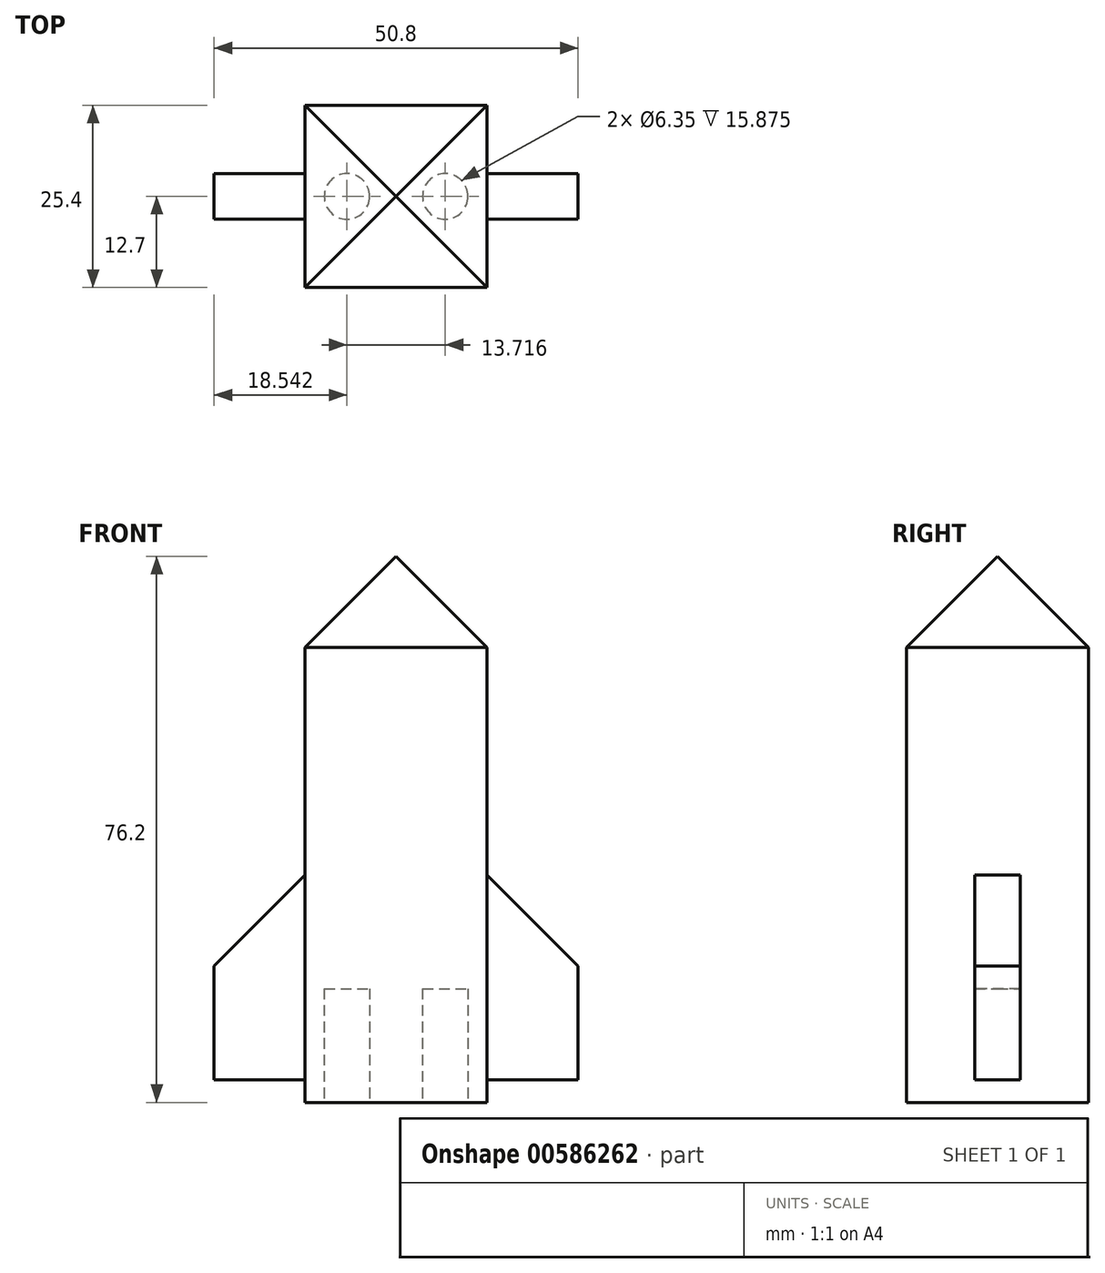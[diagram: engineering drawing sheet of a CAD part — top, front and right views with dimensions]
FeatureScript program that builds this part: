
annotation { "Feature Type Name" : "Feature", "Feature Type Description" : "" }
export const myFeature = defineFeature(function(context is Context, id is Id, definition is map)
    precondition{}
    {
        {
            var Q0;
            Q0=qCreatedBy(makeId("Front.planeOp"),FACE);
            var sketch = newSketch(context, id + "F0", { "sketchPlane" : qUnion([Q0])});
            skLineSegment(sketch, "E0.bottom", {"start": v(-25.4, 0) * mm, "end": v(25.4, 0) * mm, "construction": true});
            skLineSegment(sketch, "E0.top", {"start": v(-25.4, 76.2) * mm, "end": v(25.4, 76.2) * mm, "construction": true});
            skLineSegment(sketch, "E0.left", {"start": v(-25.4, 0) * mm, "end": v(-25.4, 76.2) * mm, "construction": true});
            skLineSegment(sketch, "E0.right", {"start": v(25.4, 0) * mm, "end": v(25.4, 76.2) * mm, "construction": true});
            skLineSegment(sketch, "E1", {"start": v(0, 0) * mm, "end": v(0, 76.2) * mm, "construction": true});
            skLineSegment(sketch, "E2", {"start": v(0, 76.2) * mm, "end": v(-12.7, 63.5) * mm});
            skLineSegment(sketch, "E3", {"start": v(-12.7, 63.5) * mm, "end": v(-12.7, 31.75) * mm});
            skLineSegment(sketch, "E4", {"start": v(-12.7, 31.75) * mm, "end": v(-25.4, 19.05) * mm});
            skLineSegment(sketch, "E5", {"start": v(-25.4, 3.18) * mm, "end": v(-12.7, 3.18) * mm});
            skLineSegment(sketch, "E6", {"start": v(-12.7, 3.18) * mm, "end": v(-12.7, 0) * mm});
            skLineSegment(sketch, "E7", {"start": v(-12.7, 0) * mm, "end": v(0, 0) * mm});
            skLineSegment(sketch, "E8", {"start": v(-25.4, 19.05) * mm, "end": v(-25.4, 3.18) * mm});
            skLineSegment(sketch, "E9.MirrorCS", {"start": v(12.7, 0) * mm, "end": v(0, 0) * mm});
            skLineSegment(sketch, "E10.MirrorCS", {"start": v(12.7, 3.18) * mm, "end": v(12.7, 0) * mm});
            skLineSegment(sketch, "E11.MirrorCS", {"start": v(25.4, 3.17) * mm, "end": v(12.7, 3.18) * mm});
            skLineSegment(sketch, "E12.MirrorCS", {"start": v(25.4, 19.05) * mm, "end": v(25.4, 3.18) * mm});
            skLineSegment(sketch, "E13.MirrorCS", {"start": v(12.7, 31.75) * mm, "end": v(25.4, 19.05) * mm});
            skLineSegment(sketch, "E14.MirrorCS", {"start": v(0, 76.2) * mm, "end": v(12.7, 63.5) * mm});
            skLineSegment(sketch, "E15.MirrorCS", {"start": v(12.7, 63.5) * mm, "end": v(12.7, 31.75) * mm});
            skSolve(sketch);
        }
        {
            var Q0;
            Q0=makeQuery(id+"F0.imprint","IMPRINT",FACE,{"disambiguationData":[TD([[makeQuery(id+"F0.imprint","IMPRINT",EDGE,{"derivedFrom":sQuery(id+"F0.wireOp",EDGE,"E0.bottom")}),1.0]])]});
            var Q1;
            Q1=makeQuery(id+"F0.imprint","IMPRINT",FACE,{"disambiguationData":[TD([[makeQuery(id+"F0.imprint","IMPRINT",EDGE,{"derivedFrom":sQuery(id+"F0.wireOp",EDGE,"E2")}),1.0]])]});
            extrude(context, id + "F1", {"entities" : qUnion([Q0, Q1]), "endBound" : BoundingType.SYMMETRIC, "depth" : 25.4 * mm, "offsetDistance" : 25.4 * mm});
        }
        {
            var Q0;
            Q0=makeQuery(id+"F1.opExtrude","SWEPT_FACE",FACE,{"disambiguationData":[OSD([sQuery(id+"F0.wireOp",EDGE,"E15.MirrorCS")])]});
            var sketch = newSketch(context, id + "F2", { "sketchPlane" : qUnion([Q0])});
            skLineSegment(sketch, "E16.bottom", {"start": v(12.7, 0) * mm, "end": v(-12.7, 0) * mm});
            skLineSegment(sketch, "E16.top", {"start": v(12.7, 76.2) * mm, "end": v(-12.7, 76.2) * mm});
            skLineSegment(sketch, "E16.left", {"start": v(12.7, 0) * mm, "end": v(12.7, 76.2) * mm});
            skLineSegment(sketch, "E16.right", {"start": v(-12.7, 0) * mm, "end": v(-12.7, 76.2) * mm});
            skLineSegment(sketch, "E17.bottom", {"start": v(3.18, 3.18) * mm, "end": v(-3.17, 3.18) * mm});
            skLineSegment(sketch, "E17.top", {"start": v(3.17, 31.75) * mm, "end": v(-3.17, 31.75) * mm});
            skLineSegment(sketch, "E17.left", {"start": v(3.18, 3.18) * mm, "end": v(3.18, 31.75) * mm});
            skLineSegment(sketch, "E17.right", {"start": v(-3.17, 3.18) * mm, "end": v(-3.17, 31.75) * mm});
            skSolve(sketch);
        }
        {
            var Q0;
            Q0 = qSketchRegion(id + "F2", true);
            extrude(context, id + "F3", {"entities" : qUnion([Q0]), "operationType" : NewBodyOperationType.REMOVE, "endBound" : BoundingType.THROUGH_ALL, "depth" : 25.4 * mm, "offsetDistance" : 25.4 * mm});
        }
        {
            var Q0;
            Q0=makeQuery(id+"F1.opExtrude","SWEPT_FACE",FACE,{"disambiguationData":[OSD([sQuery(id+"F0.wireOp",EDGE,"E3")])]});
            var sketch = newSketch(context, id + "F4", { "sketchPlane" : qUnion([Q0])});
            skLineSegment(sketch, "E18.bottom", {"start": v(-3.17, 3.18) * mm, "end": v(3.17, 3.18) * mm});
            skLineSegment(sketch, "E18.top", {"start": v(-3.17, 31.75) * mm, "end": v(3.17, 31.75) * mm});
            skLineSegment(sketch, "E18.left", {"start": v(-3.17, 3.18) * mm, "end": v(-3.17, 31.75) * mm});
            skLineSegment(sketch, "E18.right", {"start": v(3.18, 3.18) * mm, "end": v(3.18, 31.75) * mm});
            skLineSegment(sketch, "E19.bottom", {"start": v(-12.7, 3.18) * mm, "end": v(12.7, 3.18) * mm});
            skLineSegment(sketch, "E19.top", {"start": v(-12.7, 31.75) * mm, "end": v(12.7, 31.75) * mm});
            skLineSegment(sketch, "E19.left", {"start": v(-12.7, 3.18) * mm, "end": v(-12.7, 31.75) * mm});
            skLineSegment(sketch, "E19.right", {"start": v(12.7, 3.18) * mm, "end": v(12.7, 31.75) * mm});
            skSolve(sketch);
        }
        {
            var Q0;
            {var subQ0=sQuery(id+"F4.wireOp",EDGE,"E18.left");Q0=makeQuery(id+"F4.imprint","IMPRINT",FACE,{"disambiguationData":[TD([[makeQuery(id+"F4.imprint","IMPRINT",EDGE,{"derivedFrom":subQ0}),1.0]])]});}
            var Q1;
            {var subQ0=sQuery(id+"F4.wireOp",EDGE,"E18.right");Q1=makeQuery(id+"F4.imprint","IMPRINT",FACE,{"disambiguationData":[TD([[makeQuery(id+"F4.imprint","IMPRINT",EDGE,{"derivedFrom":subQ0}),-1.0]])]});}
            extrude(context, id + "F5", {"entities" : qUnion([Q0, Q1]), "operationType" : NewBodyOperationType.REMOVE, "endBound" : BoundingType.THROUGH_ALL, "depth" : 25.4 * mm, "offsetDistance" : 25.4 * mm});
        }
        {
            var Q0;
            Q0=makeQuery(id+"F3.boolean.opBoolean","MERGE",FACE,{"derivedFrom":[makeQuery(id+"F1.opExtrude","SWEPT_FACE",FACE,{"disambiguationData":[OSD([sQuery(id+"F0.wireOp",EDGE,"E10.MirrorCS")])]}),makeQuery(id+"F1.opExtrude","SWEPT_FACE",FACE,{"disambiguationData":[OSD([sQuery(id+"F0.wireOp",EDGE,"E15.MirrorCS")])]}),makeQuery(id+"F3.opExtrude","CAP_FACE",FACE,{"disambiguationData":[OSD([sQuery(id+"F2.wireOp",EDGE,"E16.bottom"),sQuery(id+"F2.wireOp",EDGE,"E16.top"),sQuery(id+"F2.wireOp",EDGE,"E16.left"),sQuery(id+"F2.wireOp",EDGE,"E16.right"),sQuery(id+"F2.wireOp",EDGE,"E17.bottom"),sQuery(id+"F2.wireOp",EDGE,"E17.top"),sQuery(id+"F2.wireOp",EDGE,"E17.left"),sQuery(id+"F2.wireOp",EDGE,"E17.right")])],"isStart":true})]});
            var sketch = newSketch(context, id + "F6", { "sketchPlane" : qUnion([Q0])});
            skLineSegment(sketch, "E20", {"start": v(-12.7, 63.5) * mm, "end": v(0, 76.2) * mm});
            skLineSegment(sketch, "E21", {"start": v(0, 76.2) * mm, "end": v(12.7, 63.5) * mm});
            skLineSegment(sketch, "E22", {"start": v(-12.7, 63.5) * mm, "end": v(-12.7, 76.2) * mm});
            skLineSegment(sketch, "E23", {"start": v(-12.7, 76.2) * mm, "end": v(12.7, 76.2) * mm});
            skLineSegment(sketch, "E24", {"start": v(12.7, 76.2) * mm, "end": v(12.7, 63.5) * mm});
            skSolve(sketch);
        }
        {
            var Q0;
            Q0 = qSketchRegion(id + "F6", true);
            extrude(context, id + "F7", {"entities" : qUnion([Q0]), "operationType" : NewBodyOperationType.REMOVE, "endBound" : BoundingType.THROUGH_ALL, "oppositeDirection" : true, "depth" : 25.4 * mm, "offsetDistance" : 25.4 * mm});
        }
        {
            var Q0;
            Q0=makeQuery(id+"F1.opExtrude","SWEPT_FACE",FACE,{"disambiguationData":[OSD([sQuery(id+"F0.wireOp",EDGE,"E7"),sQuery(id+"F0.wireOp",EDGE,"E9.MirrorCS")])]});
            var sketch = newSketch(context, id + "F8", { "sketchPlane" : qUnion([Q0])});
            skCircle(sketch, "E25", {"center": v(6.86, 0) * mm, "radius": 3.18 * mm});
            skLineSegment(sketch, "E26", {"start": v(0, -12.7) * mm, "end": v(0, 12.7) * mm, "construction": true});
            skCircle(sketch, "E27.MirrorC", {"center": v(-6.86, 0) * mm, "radius": 3.18 * mm});
            skSolve(sketch);
        }
        {
            var Q0;
            Q0 = qSketchRegion(id + "F8", true);
            extrude(context, id + "F9", {"entities" : qUnion([Q0]), "operationType" : NewBodyOperationType.REMOVE, "oppositeDirection" : true, "depth" : 15.88 * mm, "offsetDistance" : 25.4 * mm});
        }
    });
